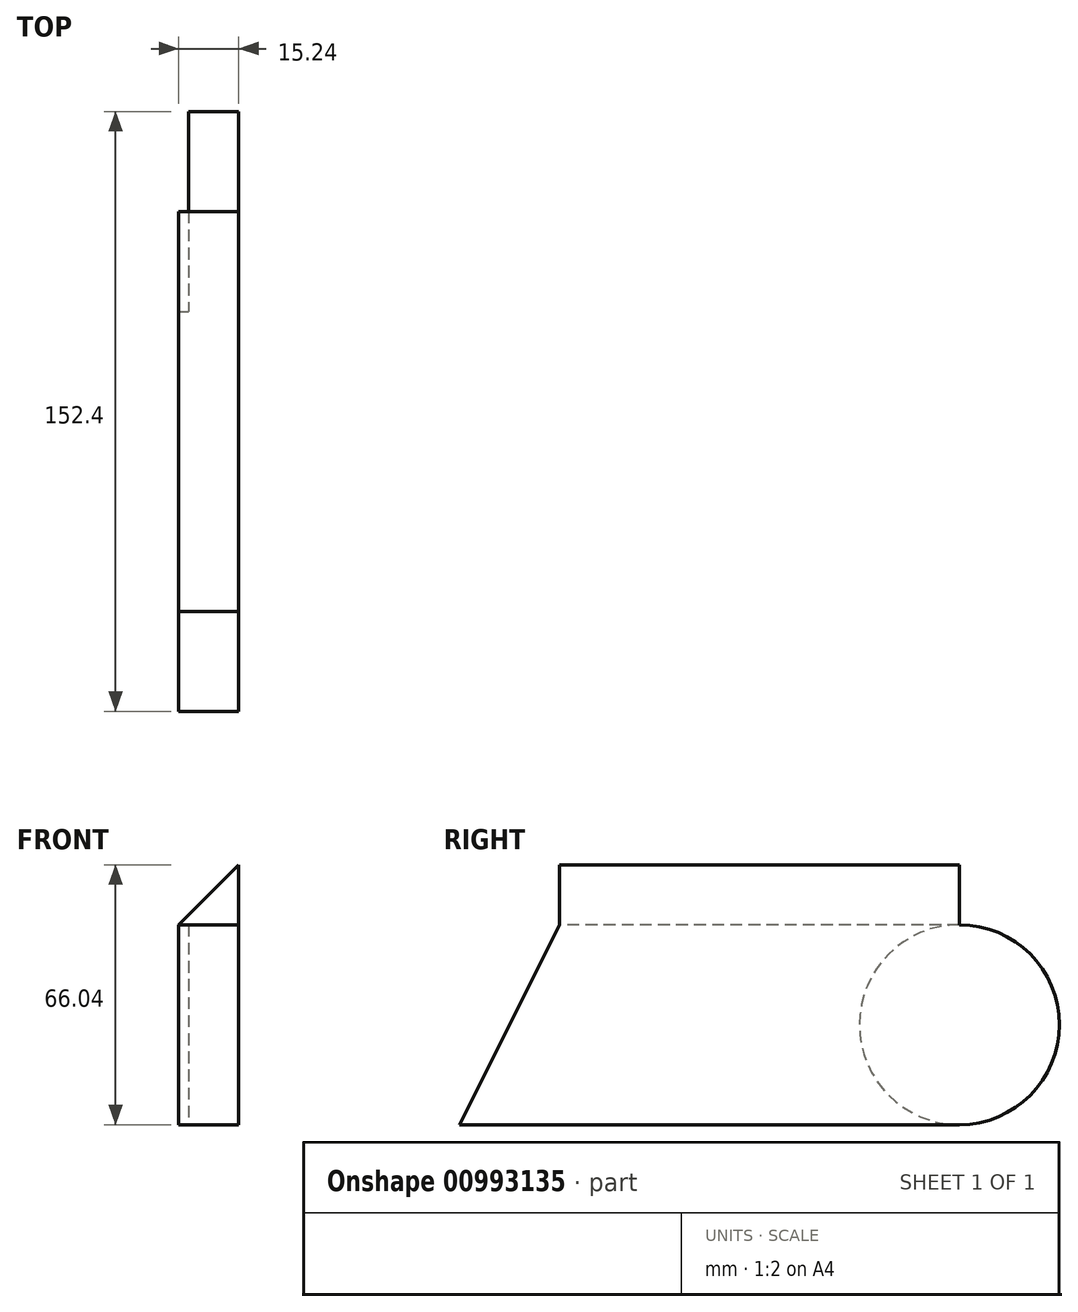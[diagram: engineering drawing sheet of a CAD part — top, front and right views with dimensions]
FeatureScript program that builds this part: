
annotation { "Feature Type Name" : "Feature", "Feature Type Description" : "" }
export const myFeature = defineFeature(function(context is Context, id is Id, definition is map)
    precondition{}
    {
        {
            var Q0;
            Q0=qCreatedBy(makeId("Right.planeOp"),FACE);
            var sketch = newSketch(context, id + "F0", { "sketchPlane" : qUnion([Q0])});
            skLineSegment(sketch, "E0", {"start": v(62.58, 20.67) * mm, "end": v(-77.12, 20.67) * mm});
            skCircle(sketch, "E1", {"center": v(37.18, 20.67) * mm, "radius": 25.4 * mm});
            skLineSegment(sketch, "E2", {"start": v(-77.12, 20.67) * mm, "end": v(-89.82, -4.73) * mm});
            skLineSegment(sketch, "E3", {"start": v(-89.82, -4.73) * mm, "end": v(37.18, -4.73) * mm});
            skPoint(sketch, "E4.startSnap0", {"position": v(-26.32, -4.73) * mm});
            skLineSegment(sketch, "E5", {"start": v(-77.12, 20.67) * mm, "end": v(-64.42, 46.07) * mm});
            skLineSegment(sketch, "E6", {"start": v(-64.42, 46.07) * mm, "end": v(37.18, 46.07) * mm});
            skSolve(sketch);
        }
        {
            var Q0;
            {var subQ4=sQuery(id+"F0.wireOp",EDGE,"E4");Q0=makeQuery(id+"F0.imprint","IMPRINT",FACE,{"disambiguationData":[TD([[makeQuery(id+"F0.imprint","IMPRINT",EDGE,{"derivedFrom":subQ4}),-1.0]])]});}
            var Q1;
            {var subQ0=sQuery(id+"F0.wireOp",EDGE,"E2");Q1=makeQuery(id+"F0.imprint","IMPRINT",FACE,{"disambiguationData":[TD([[makeQuery(id+"F0.imprint","IMPRINT",EDGE,{"derivedFrom":subQ0}),1.0]])]});}
            var Q2;
            {var subQ0=sQuery(id+"F0.wireOp",EDGE,"E5");Q2=makeQuery(id+"F0.imprint","IMPRINT",FACE,{"disambiguationData":[TD([[makeQuery(id+"F0.imprint","IMPRINT",EDGE,{"derivedFrom":subQ0}),-1.0]])]});}
            extrude(context, id + "F1", {"entities" : qUnion([Q0, Q1, Q2]), "oppositeDirection" : true, "depth" : 15.24 * mm, "offsetDistance" : 25.4 * mm});
        }
        {
            var Q0;
            {var subQ0=sQuery(id+"F0.wireOp",EDGE,"E1");var subQ1=sQuery(id+"F0.wireOp",EDGE,"E0");var subQ2=makeQuery(id+"F0.imprint","INTERSECT",VERTEX,{"disambiguationData":[OD(0.0)],"derivedFrom":[subQ1,subQ0]});Q0=makeQuery(id+"F0.imprint","IMPRINT",FACE,{"disambiguationData":[TD([[makeQuery(id+"F0.imprint","IMPRINT",EDGE,{"disambiguationData":[TD([[subQ2,-1.0]])],"derivedFrom":subQ1}),-1.0]])]});}
            var Q1;
            {var subQ0=sQuery(id+"F0.wireOp",EDGE,"E1");var subQ1=sQuery(id+"F0.wireOp",EDGE,"E0");var subQ2=makeQuery(id+"F0.imprint","INTERSECT",VERTEX,{"disambiguationData":[OD(0.0)],"derivedFrom":[subQ1,subQ0]});Q1=makeQuery(id+"F0.imprint","IMPRINT",FACE,{"disambiguationData":[TD([[makeQuery(id+"F0.imprint","IMPRINT",EDGE,{"disambiguationData":[TD([[subQ2,-1.0]])],"derivedFrom":subQ1}),1.0]])]});}
            extrude(context, id + "F2", {"entities" : qUnion([Q0, Q1]), "operationType" : NewBodyOperationType.ADD, "oppositeDirection" : true, "depth" : 12.7 * mm, "offsetDistance" : 25.4 * mm});
        }
        {
            var Q0;
            Q0=makeQuery(id+"F1.opExtrude","SWEPT_FACE",FACE,{"disambiguationData":[OSD([sQuery(id+"F0.wireOp",EDGE,"E6")])]});
            extrude(context, id + "F3", {"entities" : qUnion([Q0]), "operationType" : NewBodyOperationType.ADD, "depth" : 15.24 * mm, "offsetDistance" : 25.4 * mm});
        }
        {
            var Q0;
            Q0=makeQuery(id+"F3.opExtrude","SWEPT_FACE",FACE,{"disambiguationData":[OSD([sQuery(id+"F0.wireOp",EDGE,"E5"),sQuery(id+"F0.wireOp",EDGE,"E6")])]});
            var sketch = newSketch(context, id + "F4", { "sketchPlane" : qUnion([Q0])});
            skLineSegment(sketch, "E7", {"start": v(0, 61.3) * mm, "end": v(-15.24, 46.07) * mm});
            skSolve(sketch);
        }
        {
            var Q0;
            Q0=makeQuery(id+"F4.imprint","IMPRINT",FACE,{"disambiguationData":[TD([[makeQuery(id+"F4.imprint","IMPRINT",EDGE,{"derivedFrom":sQuery(id+"F4.wireOp",EDGE,"E7")}),-1.0]])]});
            extrude(context, id + "F5", {"entities" : qUnion([Q0]), "operationType" : NewBodyOperationType.REMOVE, "oppositeDirection" : true, "depth" : 228.6 * mm, "offsetDistance" : 25.4 * mm});
        }
    });
